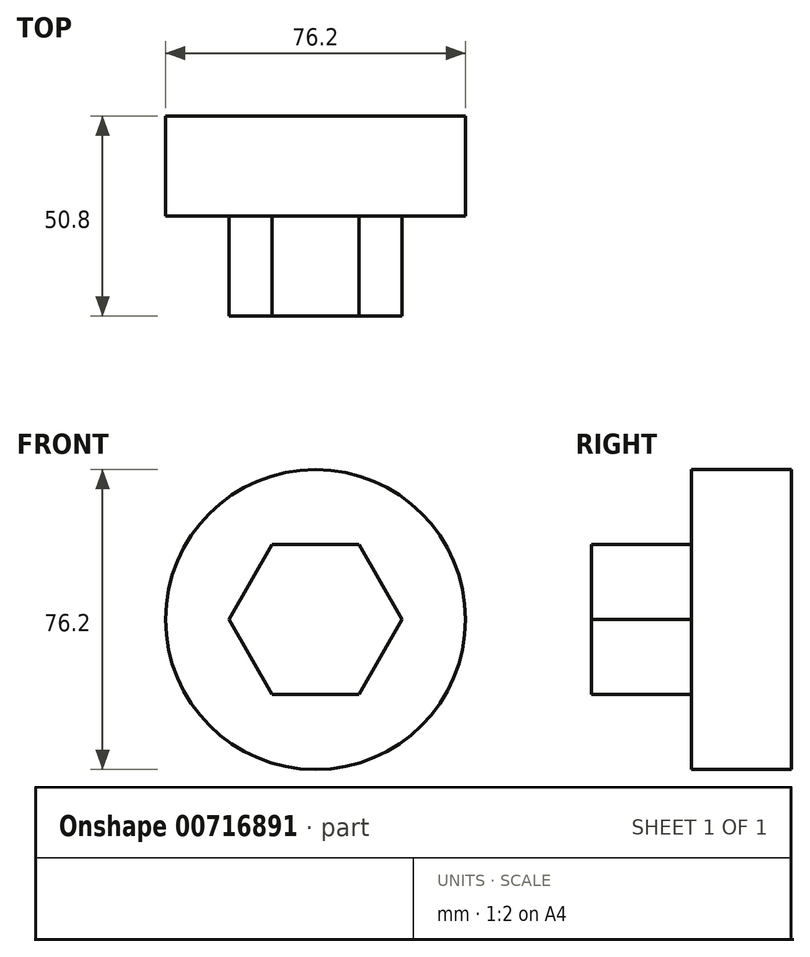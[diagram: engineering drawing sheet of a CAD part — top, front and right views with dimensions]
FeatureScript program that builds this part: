
annotation { "Feature Type Name" : "Feature", "Feature Type Description" : "" }
export const myFeature = defineFeature(function(context is Context, id is Id, definition is map)
    precondition{}
    {
        {
            var Q0;
            Q0=qCreatedBy(makeId("Front.planeOp"),FACE);
            var sketch = newSketch(context, id + "F0", { "sketchPlane" : qUnion([Q0])});
            skCircle(sketch, "E0", {"center": v(0, 0) * mm, "radius": 38.1 * mm});
            skSolve(sketch);
        }
        {
            var Q0;
            Q0=makeQuery(id+"F0.imprint","IMPRINT",FACE,{"disambiguationData":[TD([[makeQuery(id+"F0.imprint","IMPRINT",EDGE,{"derivedFrom":sQuery(id+"F0.wireOp",EDGE,"E0")}),1.0]])]});
            extrude(context, id + "F1", {"entities" : qUnion([Q0]), "flatOperationType" : FlatOperationType.REMOVE, "depth" : 25.4 * mm, "offsetDistance" : 25.4 * mm, "domain" : OperationDomain.MODEL, "symmetric" : true});
        }
        {
            var Q0;
            Q0=makeQuery(id+"F1.opExtrude","CAP_FACE",FACE,{"disambiguationData":[OSD([sQuery(id+"F0.wireOp",EDGE,"E0")])],"isStart":false});
            var sketch = newSketch(context, id + "F2", { "sketchPlane" : qUnion([Q0])});
            skCircle(sketch, "E1.cCircle", {"center": v(0, 0) * mm, "radius": 19.05 * mm, "construction": true});
            skLineSegment(sketch, "E1.0", {"start": v(-11, 19.05) * mm, "end": v(11, 19.05) * mm});
            skLineSegment(sketch, "E1.1", {"start": v(11, 19.05) * mm, "end": v(22, 0) * mm});
            skLineSegment(sketch, "E1.2", {"start": v(22, 0) * mm, "end": v(11, -19.05) * mm});
            skLineSegment(sketch, "E1.3", {"start": v(11, -19.05) * mm, "end": v(-11, -19.05) * mm});
            skLineSegment(sketch, "E1.4", {"start": v(-11, -19.05) * mm, "end": v(-22, 0) * mm});
            skLineSegment(sketch, "E1.5", {"start": v(-22, 0) * mm, "end": v(-11, 19.05) * mm});
            skPoint(sketch, "E1.0.midPoint", {"position": v(0, 19.05) * mm});
            skSolve(sketch);
        }
        {
            var Q0;
            Q0=makeQuery(id+"F2.imprint","IMPRINT",FACE,{"disambiguationData":[TD([[makeQuery(id+"F2.imprint","IMPRINT",EDGE,{"derivedFrom":sQuery(id+"F2.wireOp",EDGE,"E1.0")}),-1.0]])]});
            extrude(context, id + "F3", {"entities" : qUnion([Q0]), "operationType" : NewBodyOperationType.ADD, "depth" : 25.4 * mm, "offsetDistance" : 25.4 * mm});
        }
    });
